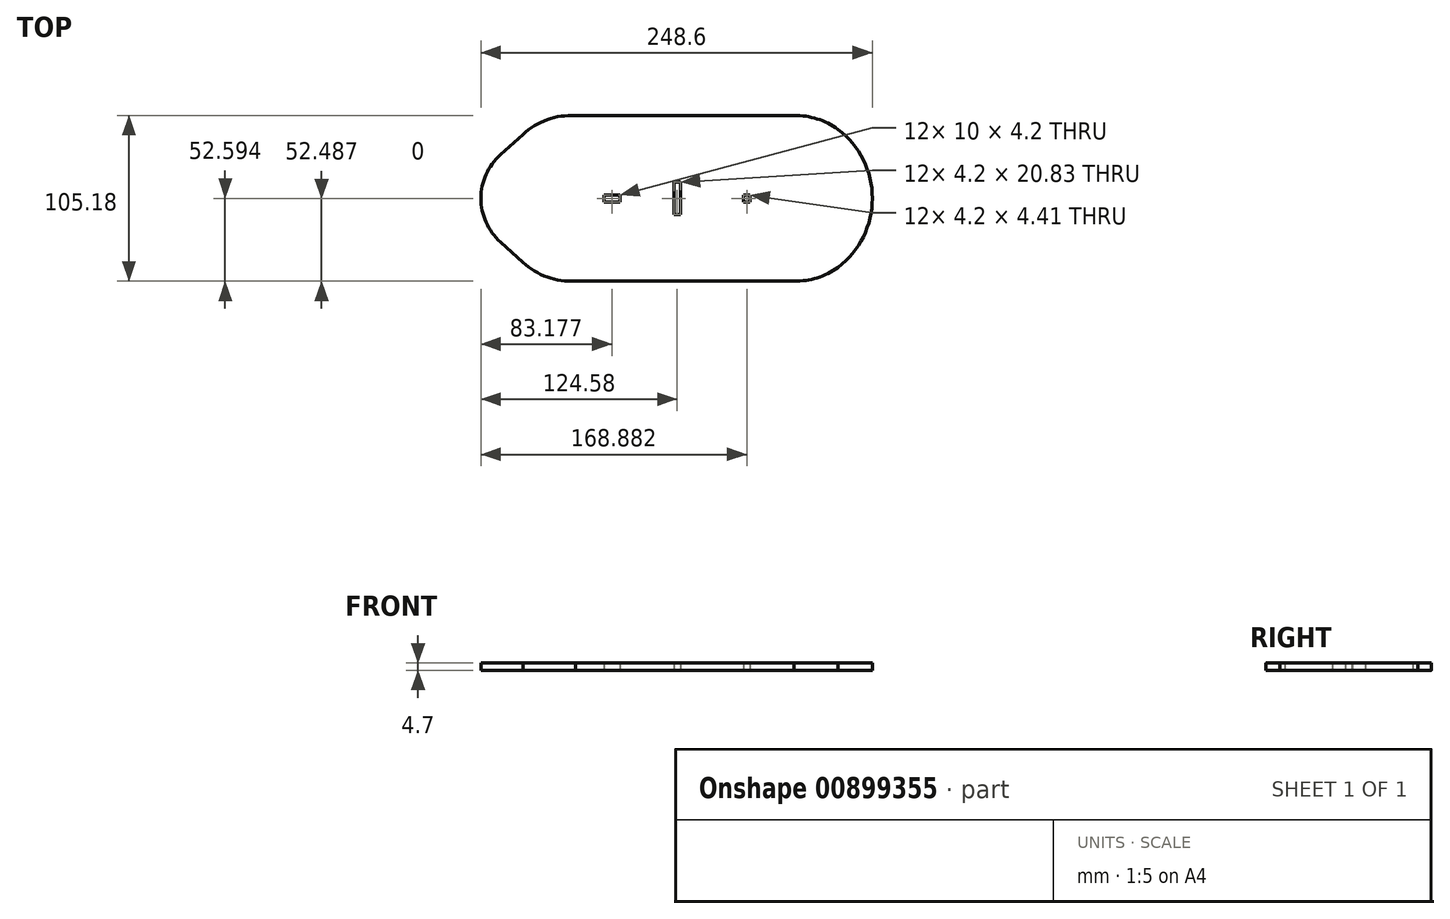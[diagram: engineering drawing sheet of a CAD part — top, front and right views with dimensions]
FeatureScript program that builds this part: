
annotation { "Feature Type Name" : "Feature", "Feature Type Description" : "" }
export const myFeature = defineFeature(function(context is Context, id is Id, definition is map)
    precondition{}
    {
        {
            var Q0;
            Q0=qCreatedBy(makeId("Top.planeOp"),FACE);
            var sketch = newSketch(context, id + "F0", { "sketchPlane" : qUnion([Q0])});
            skPoint(sketch, "E0.middle", {"position": v(-5.9, -300.47) * mm});
            skPoint(sketch, "E1.endSnap0", {"position": v(-80.9, -300.47) * mm});
            skPoint(sketch, "E2", {"position": v(-9.6, -300.47) * mm});
            skPoint(sketch, "E3", {"position": v(-51, -300.57) * mm});
            skPoint(sketch, "E4", {"position": v(34.92, -300.47) * mm});
            skLineSegment(sketch, "E5.bottom", {"start": v(-56, -298.47) * mm, "end": v(-46, -298.47) * mm});
            skLineSegment(sketch, "E5.top", {"start": v(-56, -302.67) * mm, "end": v(-46, -302.67) * mm});
            skLineSegment(sketch, "E5.left", {"start": v(-56, -298.47) * mm, "end": v(-56, -302.67) * mm});
            skLineSegment(sketch, "E5.right", {"start": v(-46, -298.47) * mm, "end": v(-46, -302.67) * mm});
            skLineSegment(sketch, "E6.MirrorCS", {"start": v(32.61, -298.26) * mm, "end": v(32.61, -302.67) * mm});
            skLineSegment(sketch, "E7.MirrorCS", {"start": v(36.81, -298.26) * mm, "end": v(36.81, -302.67) * mm});
            skLineSegment(sketch, "E8.bottom", {"start": v(-11.7, -290.05) * mm, "end": v(-7.5, -290.05) * mm});
            skLineSegment(sketch, "E8.top", {"start": v(-11.7, -310.88) * mm, "end": v(-7.5, -310.88) * mm});
            skLineSegment(sketch, "E8.left", {"start": v(-11.7, -290.05) * mm, "end": v(-11.7, -310.88) * mm});
            skLineSegment(sketch, "E8.right", {"start": v(-7.5, -290.05) * mm, "end": v(-7.5, -310.88) * mm});
            skPoint(sketch, "E9.orphan", {"position": v(-80.9, -282.97) * mm});
            skPoint(sketch, "E10.orphan", {"position": v(-80.9, -317.97) * mm});
            skArc(sketch, "E11.4", {"start": v(74.82, -280.77) * mm, "mid": v(74.79, -280.74) * mm, "end": v(74.75, -280.72) * mm});
            skArc(sketch, "E12.0", {"start": v(-74.16, -247.97) * mm, "mid": v(-92.02, -250.47) * mm, "end": v(-107.46, -259.8) * mm});
            skLineSegment(sketch, "E12.1", {"start": v(-107.46, -259.8) * mm, "end": v(-121.83, -272.74) * mm});
            skLineSegment(sketch, "E12.2", {"start": v(-74.16, -247.97) * mm, "end": v(64.65, -247.97) * mm});
            skArc(sketch, "E12.3", {"start": v(-121.83, -272.74) * mm, "mid": v(-134.17, -300.47) * mm, "end": v(-121.83, -328.2) * mm});
            skLineSegment(sketch, "E12.4", {"start": v(-121.83, -328.2) * mm, "end": v(-107.46, -341.14) * mm});
            skArc(sketch, "E12.5", {"start": v(-74.16, -352.97) * mm, "mid": v(-92.02, -350.47) * mm, "end": v(-107.46, -341.14) * mm});
            skArc(sketch, "E12.6", {"start": v(92.67, -256.65) * mm, "mid": v(79.38, -249.96) * mm, "end": v(64.65, -247.97) * mm});
            skArc(sketch, "E12.7", {"start": v(92.67, -344.28) * mm, "mid": v(114.43, -300.47) * mm, "end": v(92.67, -256.65) * mm});
            skArc(sketch, "E12.8", {"start": v(92.67, -344.28) * mm, "mid": v(79.38, -350.97) * mm, "end": v(64.65, -352.97) * mm});
            skLineSegment(sketch, "E12.9", {"start": v(-74.16, -352.97) * mm, "end": v(64.65, -352.97) * mm});
            skPoint(sketch, "E13.MirrorCS.end.orphan", {"position": v(65.39, -317.97) * mm});
            skPoint(sketch, "E14.orphan", {"position": v(71.78, -316.2) * mm});
            skPoint(sketch, "E15.orphan", {"position": v(71.78, -284.74) * mm});
            skPoint(sketch, "E16.end.orphan", {"position": v(65.39, -282.97) * mm});
            skLineSegment(sketch, "E17", {"start": v(32.61, -298.26) * mm, "end": v(36.81, -298.26) * mm});
            skLineSegment(sketch, "E18", {"start": v(36.81, -302.67) * mm, "end": v(32.61, -302.67) * mm});
            skSolve(sketch);
        }
        {
            var Q0;
            Q0 = qSketchRegion(id + "F0", true);
            extrude(context, id + "F1", {"entities" : qUnion([Q0]), "depth" : 4.7 * mm, "offsetDistance" : 25 * mm});
        }
    });
